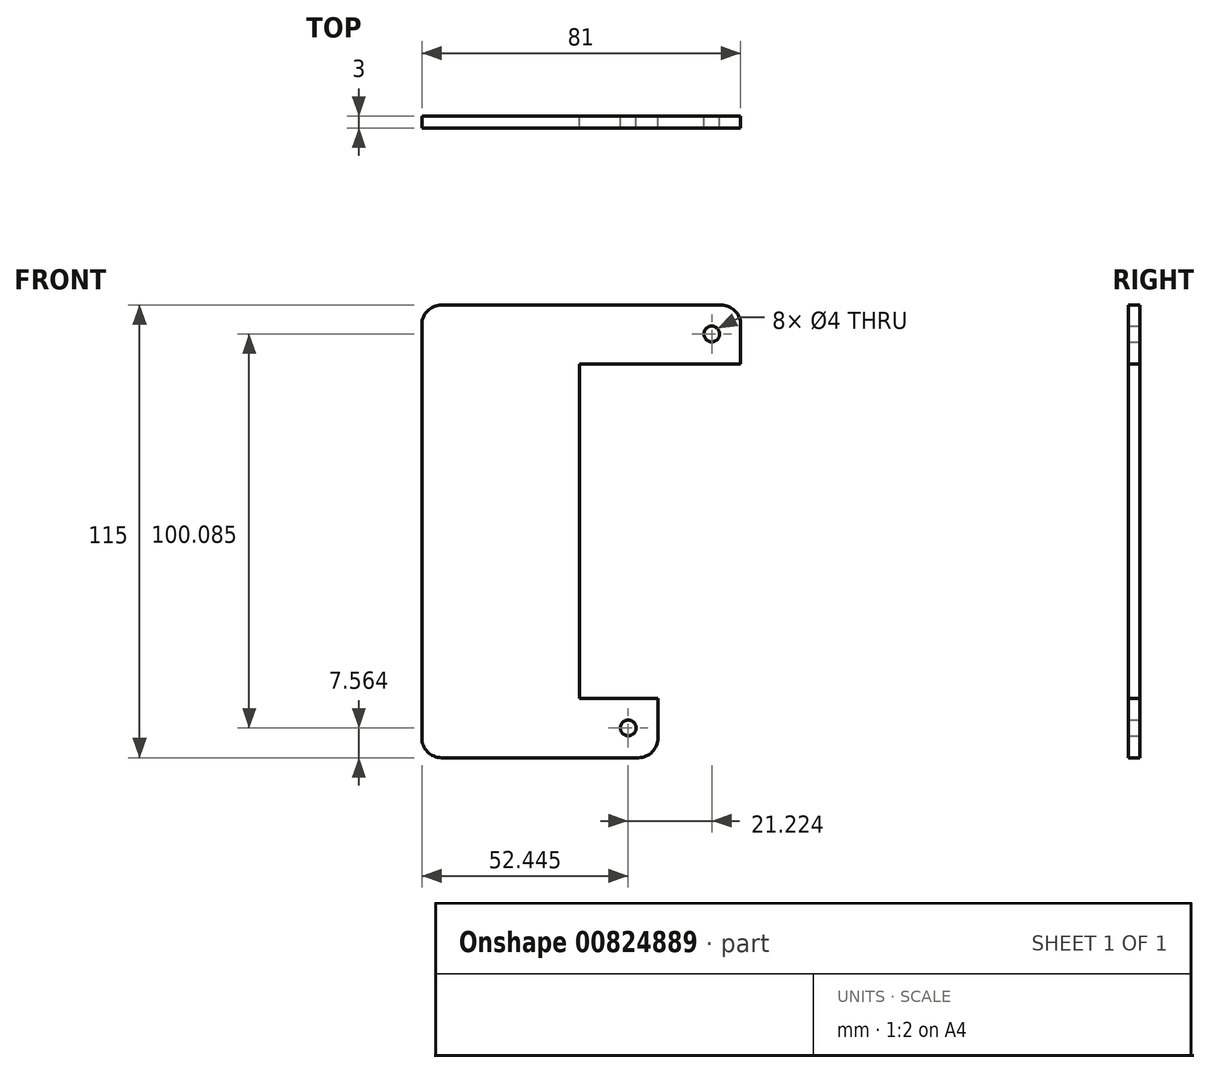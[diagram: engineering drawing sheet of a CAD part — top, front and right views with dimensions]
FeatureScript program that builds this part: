
annotation { "Feature Type Name" : "Feature", "Feature Type Description" : "" }
export const myFeature = defineFeature(function(context is Context, id is Id, definition is map)
    precondition{}
    {
        {
            var Q0;
            Q0=qCreatedBy(makeId("Front.planeOp"),FACE);
            var sketch = newSketch(context, id + "F0", { "sketchPlane" : qUnion([Q0])});
            skLineSegment(sketch, "E0", {"start": v(-81, -63.47) * mm, "end": v(-81, 51.53) * mm});
            skLineSegment(sketch, "E1", {"start": v(-81, 51.53) * mm, "end": v(0, 51.53) * mm});
            skLineSegment(sketch, "E2", {"start": v(0, 51.53) * mm, "end": v(0, 36.53) * mm});
            skLineSegment(sketch, "E3", {"start": v(0, 36.53) * mm, "end": v(-41, 36.53) * mm});
            skLineSegment(sketch, "E4", {"start": v(-41, 36.53) * mm, "end": v(-41, -48.47) * mm});
            skLineSegment(sketch, "E5", {"start": v(-41, -48.47) * mm, "end": v(-21, -48.47) * mm});
            skLineSegment(sketch, "E6", {"start": v(-21, -48.47) * mm, "end": v(-21, -63.47) * mm});
            skLineSegment(sketch, "E7", {"start": v(-21, -63.47) * mm, "end": v(-81, -63.47) * mm});
            skLineSegment(sketch, "E8", {"start": v(-41, -15.97) * mm, "end": v(-41, -15.97) * mm});
            skLineSegment(sketch, "E9", {"start": v(-41, -15.97) * mm, "end": v(-41, 4.03) * mm});
            skLineSegment(sketch, "E10", {"start": v(-41, 4.03) * mm, "end": v(-41, 4.03) * mm});
            skLineSegment(sketch, "E11", {"start": v(-41, 4.03) * mm, "end": v(-41, 36.53) * mm, "construction": true});
            skLineSegment(sketch, "E12", {"start": v(-41, -15.97) * mm, "end": v(-41, -48.47) * mm, "construction": true});
            skCircle(sketch, "E13", {"center": v(-7.33, 44.18) * mm, "radius": 2 * mm});
            skCircle(sketch, "E14", {"center": v(-28.55, -55.9) * mm, "radius": 2 * mm});
            skSolve(sketch);
        }
        {
            var Q0;
            Q0=makeQuery(id+"F0.imprint","IMPRINT",FACE,{"disambiguationData":[TD([[makeQuery(id+"F0.imprint","IMPRINT",EDGE,{"derivedFrom":sQuery(id+"F0.wireOp",EDGE,"E0")}),-1.0]])]});
            var Q1;
            {var subQ0=sQuery(id+"F0.wireOp",EDGE,"E8");Q1=makeQuery(id+"F0.imprint","IMPRINT",FACE,{"disambiguationData":[TD([[makeQuery(id+"F0.imprint","IMPRINT",EDGE,{"derivedFrom":subQ0}),1.0]])]});}
            extrude(context, id + "F1", {"entities" : qUnion([Q0, Q1]), "depth" : 3 * mm, "offsetDistance" : 25 * mm});
        }
        {
            var Q0;
            Q0=makeQuery(id+"F1.opExtrude","SWEPT_EDGE",EDGE,{"disambiguationData":[OSD([sQuery(id+"F0.wireOp",EDGE,"E0"),sQuery(id+"F0.wireOp",EDGE,"E1")])]});
            var Q1;
            Q1=makeQuery(id+"F1.opExtrude","SWEPT_EDGE",EDGE,{"disambiguationData":[OSD([sQuery(id+"F0.wireOp",EDGE,"E0"),sQuery(id+"F0.wireOp",EDGE,"E7")])]});
            var Q2;
            Q2=makeQuery(id+"F1.opExtrude","SWEPT_EDGE",EDGE,{"disambiguationData":[OSD([sQuery(id+"F0.wireOp",EDGE,"E1"),sQuery(id+"F0.wireOp",EDGE,"E2")])]});
            var Q3;
            Q3=makeQuery(id+"F1.opExtrude","SWEPT_EDGE",EDGE,{"disambiguationData":[OSD([sQuery(id+"F0.wireOp",EDGE,"E6"),sQuery(id+"F0.wireOp",EDGE,"E7")])]});
            fillet(context, id + "F2", {"entities" : qUnion([Q0, Q1, Q2, Q3]), "radius" : 5 * mm, "tangentPropagation" : true, "allowEdgeOverflow" : false});
        }
    });
